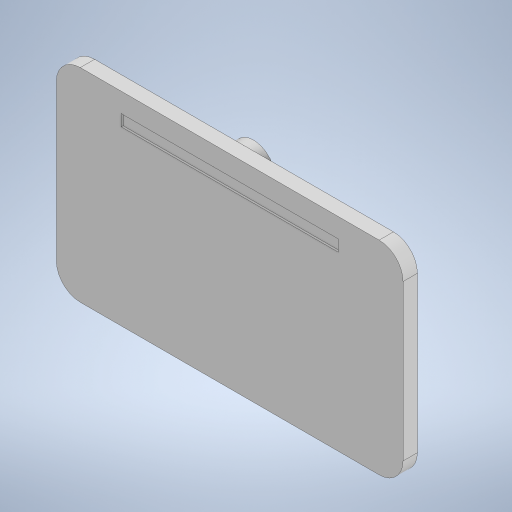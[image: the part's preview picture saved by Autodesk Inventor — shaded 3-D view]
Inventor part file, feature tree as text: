
AUTODESK INVENTOR PART (.ipt)
format: ipt  version: 2023 (Build 270158000, 158)  size: 283,136 bytes
history: native  units: mm
features: extrude x4, sketch x4, other x2, fillet x2, chamfer x1, mirror x1, projected_geometry x1
ambient origin geometry x8: Origin, YZ Plane, XZ Plane, XY Plane, X Axis, Y Axis, Z Axis, Center Point
bodies: Body1 (feature_tree)
feature tree (15):
  other  "솔리드1"
  extrude  "돌출1"  Depth=72.5mm
  extrude  "돌출2"  Depth=42.5mm
  fillet  "모깎기1"  Radius=3.0mm
  extrude  "돌출4"  Depth=4.0mm
  chamfer  "모따기1"  Distance=4.0mm
  other  "작업 평면1"
  extrude  "돌출5"  Depth=16.825mm
  mirror  "미러1"
  fillet  "모깎기2"  Radius=2.0mm
  sketch  "스케치1"
  sketch  "스케치2"
  projected_geometry  "투영된 루프1"
  sketch  "스케치5"
  sketch  "스케치6"
